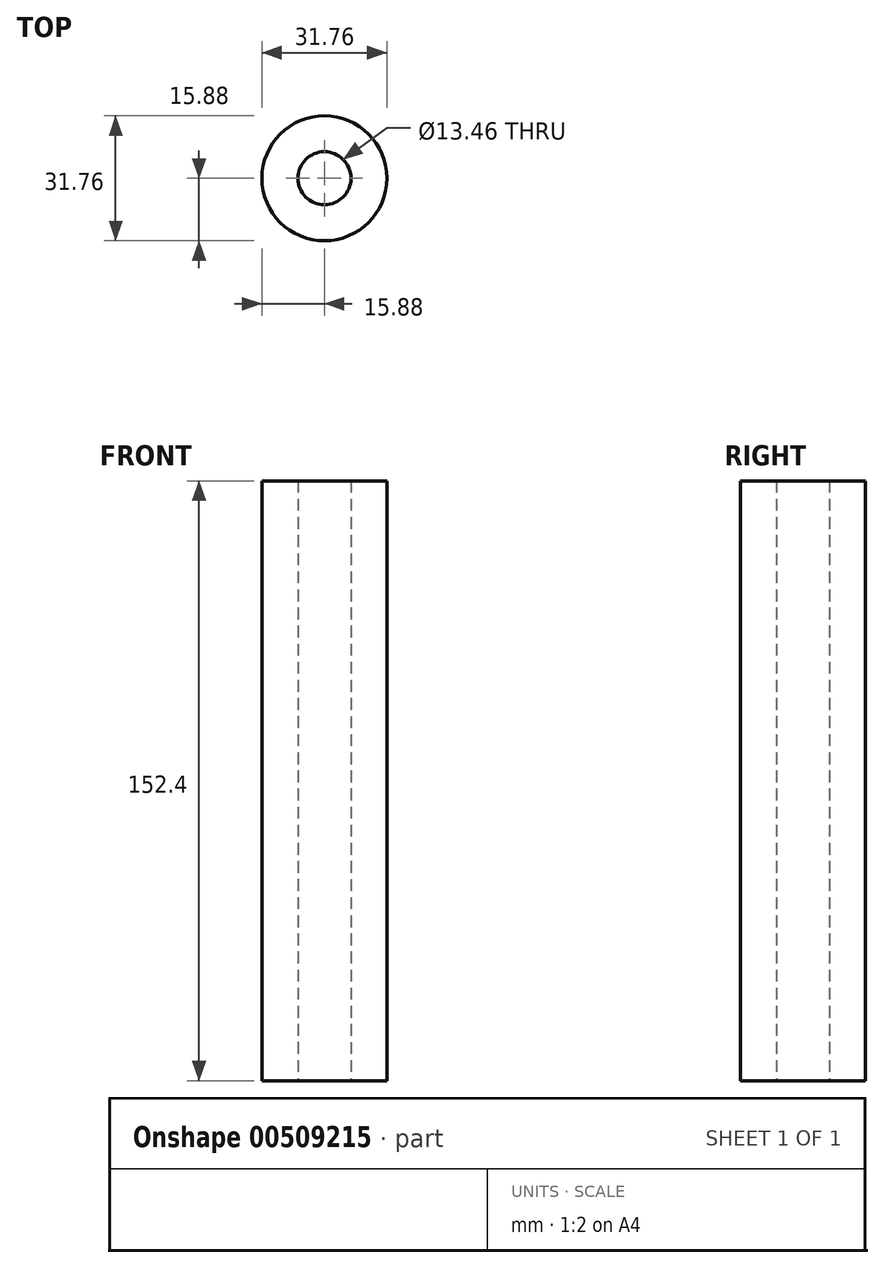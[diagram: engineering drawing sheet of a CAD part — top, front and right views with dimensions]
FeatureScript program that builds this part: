
annotation { "Feature Type Name" : "Feature", "Feature Type Description" : "" }
export const myFeature = defineFeature(function(context is Context, id is Id, definition is map)
    precondition{}
    {
        {
            var Q0;
            Q0=qCreatedBy(makeId("Top.planeOp"),FACE);
            var sketch = newSketch(context, id + "F0", { "sketchPlane" : qUnion([Q0])});
            skCircle(sketch, "E0", {"center": v(0, 0) * mm, "radius": 15.88 * mm});
            skCircle(sketch, "E1", {"center": v(0, 0) * mm, "radius": 6.73 * mm});
            skSolve(sketch);
        }
        {
            var Q0;
            Q0=makeQuery(id+"F0.imprint","IMPRINT",FACE,{"disambiguationData":[TD([[makeQuery(id+"F0.imprint","IMPRINT",EDGE,{"derivedFrom":sQuery(id+"F0.wireOp",EDGE,"E0")}),1.0]])]});
            extrude(context, id + "F1", {"entities" : qUnion([Q0]), "depth" : 152.4 * mm});
        }
    });
